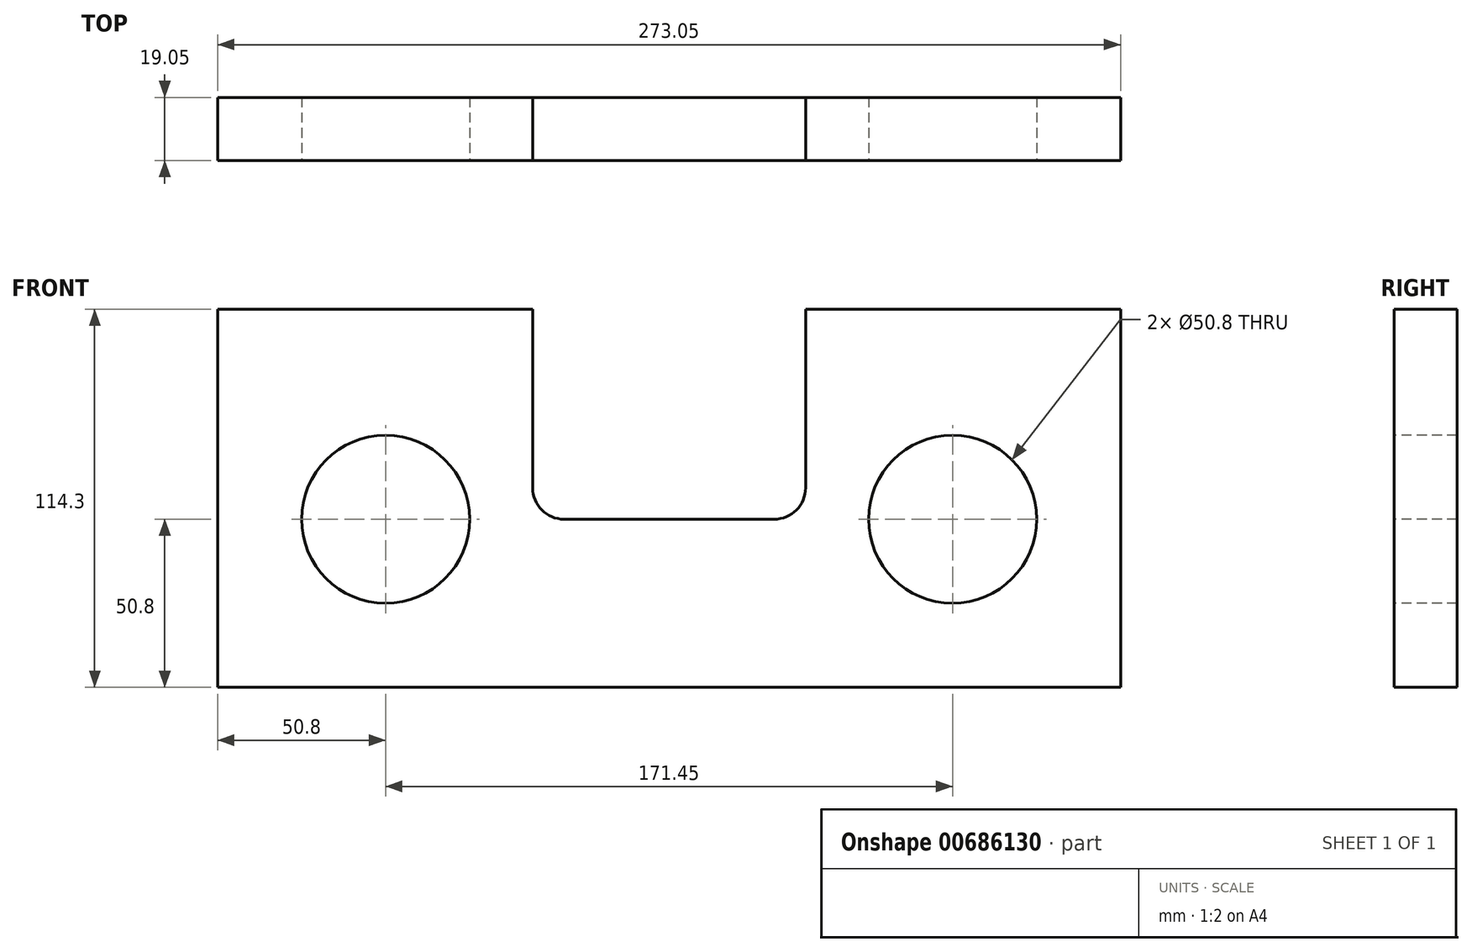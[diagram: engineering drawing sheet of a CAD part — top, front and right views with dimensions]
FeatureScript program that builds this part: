
annotation { "Feature Type Name" : "Feature", "Feature Type Description" : "" }
export const myFeature = defineFeature(function(context is Context, id is Id, definition is map)
    precondition{}
    {
        {
            var Q0;
            Q0=qCreatedBy(makeId("Front.planeOp"),FACE);
            var sketch = newSketch(context, id + "F0", { "sketchPlane" : qUnion([Q0])});
            skLineSegment(sketch, "E0.bottom", {"start": v(0, 0) * mm, "end": v(273.05, 0) * mm});
            skLineSegment(sketch, "E0.top", {"start": v(0, 114.3) * mm, "end": v(273.05, 114.3) * mm});
            skLineSegment(sketch, "E0.left", {"start": v(0, 0) * mm, "end": v(0, 114.3) * mm});
            skLineSegment(sketch, "E0.right", {"start": v(273.05, 0) * mm, "end": v(273.05, 114.3) * mm});
            skSolve(sketch);
        }
        {
            var Q0;
            Q0=makeQuery(id+"F0.imprint","IMPRINT",FACE,{"disambiguationData":[TD([[makeQuery(id+"F0.imprint","IMPRINT",EDGE,{"derivedFrom":sQuery(id+"F0.wireOp",EDGE,"E0.bottom")}),1.0]])]});
            extrude(context, id + "F1", {"entities" : qUnion([Q0]), "depth" : 19.05 * mm, "offsetDistance" : 25.4 * mm});
        }
        {
            var Q0;
            Q0=makeQuery(id+"F1.opExtrude","CAP_FACE",FACE,{"disambiguationData":[OSD([sQuery(id+"F0.wireOp",EDGE,"E0.bottom"),sQuery(id+"F0.wireOp",EDGE,"E0.top"),sQuery(id+"F0.wireOp",EDGE,"E0.left"),sQuery(id+"F0.wireOp",EDGE,"E0.right")])],"isStart":false});
            var sketch = newSketch(context, id + "F2", { "sketchPlane" : qUnion([Q0])});
            skCircle(sketch, "E1", {"center": v(50.8, 50.8) * mm, "radius": 25.4 * mm});
            skCircle(sketch, "E2", {"center": v(222.25, 50.8) * mm, "radius": 25.4 * mm});
            skSolve(sketch);
        }
        {
            var Q0;
            Q0=qSketchRegion(id+"F2",true);
            extrude(context, id + "F3", {"entities" : qUnion([Q0]), "operationType" : NewBodyOperationType.REMOVE, "oppositeDirection" : true, "depth" : 25.4 * mm, "offsetDistance" : 25.4 * mm});
        }
        {
            var Q0;
            Q0=makeQuery(id+"F1.opExtrude","CAP_FACE",FACE,{"disambiguationData":[OSD([sQuery(id+"F0.wireOp",EDGE,"E0.bottom"),sQuery(id+"F0.wireOp",EDGE,"E0.top"),sQuery(id+"F0.wireOp",EDGE,"E0.left"),sQuery(id+"F0.wireOp",EDGE,"E0.right")])],"isStart":false});
            var sketch = newSketch(context, id + "F4", { "sketchPlane" : qUnion([Q0])});
            skLineSegment(sketch, "E3", {"start": v(95.25, 114.3) * mm, "end": v(95.25, 60.32) * mm});
            skLineSegment(sketch, "E4", {"start": v(104.78, 50.8) * mm, "end": v(168.28, 50.8) * mm});
            skLineSegment(sketch, "E5", {"start": v(177.8, 60.32) * mm, "end": v(177.8, 114.3) * mm});
            skArc(sketch, "E6", {"start": v(95.25, 60.32) * mm, "mid": v(98.04, 53.59) * mm, "end": v(104.78, 50.8) * mm});
            skArc(sketch, "E7", {"start": v(168.28, 50.8) * mm, "mid": v(175.01, 53.59) * mm, "end": v(177.8, 60.32) * mm});
            skLineSegment(sketch, "E8", {"start": v(95.25, 114.3) * mm, "end": v(177.8, 114.3) * mm});
            skSolve(sketch);
        }
        {
            var Q0;
            Q0=makeQuery(id+"F4.imprint","IMPRINT",FACE,{"disambiguationData":[TD([[makeQuery(id+"F4.imprint","IMPRINT",EDGE,{"derivedFrom":sQuery(id+"F4.wireOp",EDGE,"E3")}),1.0]])]});
            extrude(context, id + "F5", {"entities" : qUnion([Q0]), "operationType" : NewBodyOperationType.REMOVE, "oppositeDirection" : true, "depth" : 25.4 * mm, "offsetDistance" : 25.4 * mm});
        }
    });
